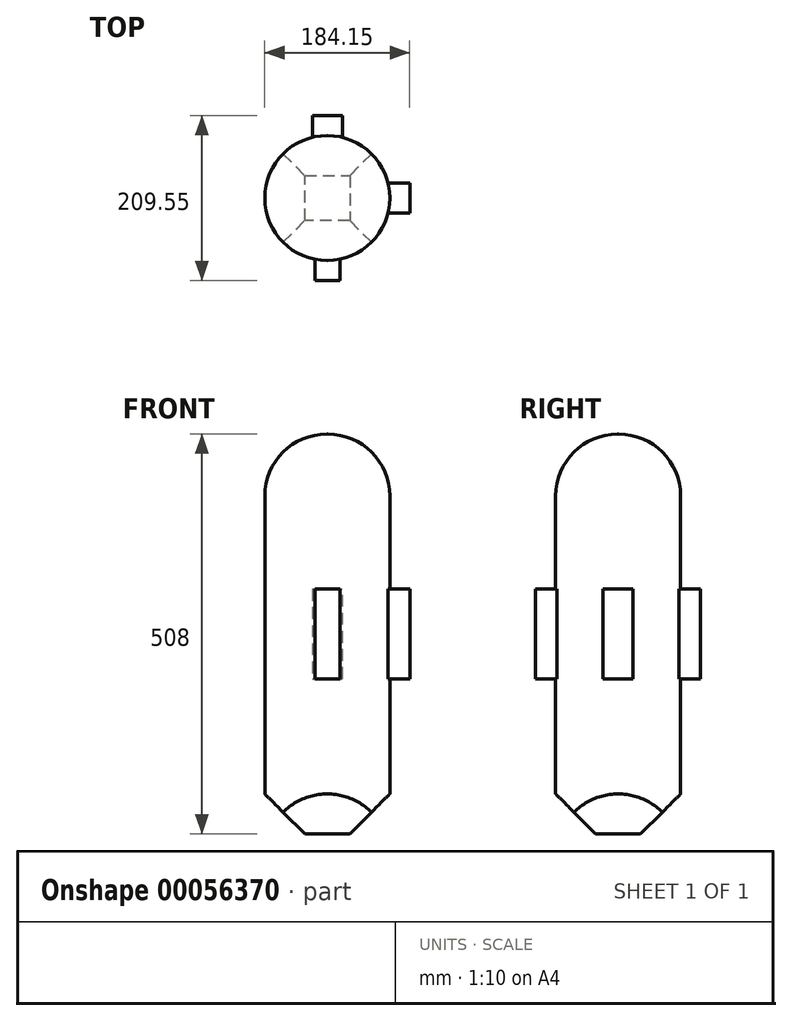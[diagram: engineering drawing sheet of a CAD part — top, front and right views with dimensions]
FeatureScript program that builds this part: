
annotation { "Feature Type Name" : "Feature", "Feature Type Description" : "" }
export const myFeature = defineFeature(function(context is Context, id is Id, definition is map)
    precondition{}
    {
        {
            var Q0;
            Q0=qCreatedBy(makeId("Front.planeOp"),FACE);
            var sketch = newSketch(context, id + "F0", { "sketchPlane" : qUnion([Q0])});
            skLineSegment(sketch, "E0.rect.bottom", {"start": v(79.37, -254) * mm, "end": v(-79.38, -254) * mm});
            skLineSegment(sketch, "E0.rect.top", {"start": v(79.37, 254) * mm, "end": v(-79.38, 254) * mm});
            skLineSegment(sketch, "E0.rect.left", {"start": v(79.37, -254) * mm, "end": v(79.37, 254) * mm});
            skLineSegment(sketch, "E0.rect.right", {"start": v(-79.38, -254) * mm, "end": v(-79.38, 254) * mm});
            skPoint(sketch, "E0.rect.middle", {"position": v(0, 0) * mm});
            skSolve(sketch);
        }
        {
            var Q0;
            Q0=makeQuery(id+"F0.imprint","IMPRINT",FACE,{"disambiguationData":[TD([[makeQuery(id+"F0.imprint","IMPRINT",EDGE,{"derivedFrom":sQuery(id+"F0.wireOp",EDGE,"E0.rect.bottom")}),-1.0]])]});
            extrude(context, id + "F1", {"entities" : qUnion([Q0]), "depth" : 158.75 * mm});
        }
        {
            var Q0;
            Q0=makeQuery(id+"F1.opExtrude","CAP_FACE",FACE,{"disambiguationData":[OSD([sQuery(id+"F0.wireOp",EDGE,"E0.rect.bottom"),sQuery(id+"F0.wireOp",EDGE,"E0.rect.top"),sQuery(id+"F0.wireOp",EDGE,"E0.rect.left"),sQuery(id+"F0.wireOp",EDGE,"E0.rect.right")])],"isStart":false});
            var sketch = newSketch(context, id + "F2", { "sketchPlane" : qUnion([Q0])});
            skLineSegment(sketch, "E1.rect.bottom", {"start": v(15.87, -57.15) * mm, "end": v(-15.88, -57.15) * mm});
            skLineSegment(sketch, "E1.rect.top", {"start": v(15.88, 57.15) * mm, "end": v(-15.87, 57.15) * mm});
            skLineSegment(sketch, "E1.rect.left", {"start": v(15.87, -57.15) * mm, "end": v(15.88, 57.15) * mm});
            skLineSegment(sketch, "E1.rect.right", {"start": v(-15.88, -57.15) * mm, "end": v(-15.87, 57.15) * mm});
            skPoint(sketch, "E1.rect.middle", {"position": v(0, 0) * mm});
            skSolve(sketch);
        }
        {
            var Q0;
            Q0=makeQuery(id+"F1.opExtrude","SWEPT_FACE",FACE,{"disambiguationData":[OSD([sQuery(id+"F0.wireOp",EDGE,"E0.rect.left")])]});
            var sketch = newSketch(context, id + "F3", { "sketchPlane" : qUnion([Q0])});
            skLineSegment(sketch, "E2.rect.bottom", {"start": v(-60.33, -57.15) * mm, "end": v(-98.43, -57.15) * mm});
            skLineSegment(sketch, "E2.rect.top", {"start": v(-60.33, 57.15) * mm, "end": v(-98.43, 57.15) * mm});
            skLineSegment(sketch, "E2.rect.left", {"start": v(-60.33, -57.15) * mm, "end": v(-60.33, 57.15) * mm});
            skLineSegment(sketch, "E2.rect.right", {"start": v(-98.43, -57.15) * mm, "end": v(-98.43, 57.15) * mm});
            skPoint(sketch, "E2.rect.middle", {"position": v(-79.38, 0) * mm});
            skPoint(sketch, "E2.rect.middle.positionSnap0", {"position": v(-79.38, 254) * mm});
            skPoint(sketch, "E2.rect.centerSnap0", {"position": v(-79.38, 254) * mm});
            skSolve(sketch);
        }
        {
            var Q0;
            Q0=makeQuery(id+"F3.imprint","IMPRINT",FACE,{"disambiguationData":[TD([[makeQuery(id+"F3.imprint","IMPRINT",EDGE,{"derivedFrom":sQuery(id+"F3.wireOp",EDGE,"E2.rect.bottom")}),-1.0]])]});
            extrude(context, id + "F4", {"entities" : qUnion([Q0]), "operationType" : NewBodyOperationType.ADD, "depth" : 25.4 * mm});
        }
        {
            var Q0;
            Q0=makeQuery(id+"F2.imprint","IMPRINT",FACE,{"disambiguationData":[TD([[makeQuery(id+"F2.imprint","IMPRINT",EDGE,{"derivedFrom":sQuery(id+"F2.wireOp",EDGE,"E1.rect.bottom")}),-1.0]])]});
            extrude(context, id + "F5", {"entities" : qUnion([Q0]), "operationType" : NewBodyOperationType.ADD, "depth" : 25.4 * mm});
        }
        {
            var Q0;
            Q0=makeQuery(id+"F1.opExtrude","SWEPT_FACE",FACE,{"disambiguationData":[OSD([sQuery(id+"F0.wireOp",EDGE,"E0.rect.top")])]});
            fillet(context, id + "F6", {"entities" : qUnion([Q0]), "radius" : 78.74 * mm, "tangentPropagation" : true, "allowEdgeOverflow" : false});
        }
        {
            var Q0;
            Q0=makeQuery(id+"F1.opExtrude","SWEPT_FACE",FACE,{"disambiguationData":[OSD([sQuery(id+"F0.wireOp",EDGE,"E0.rect.bottom")])]});
            chamfer(context, id + "F7", {"entities" : qUnion([Q0]), "width" : 50.8 * mm, "tangentPropagation" : true});
        }
        {
            var Q0;
            Q0=makeQuery(id+"F1.opExtrude","CAP_FACE",FACE,{"disambiguationData":[OSD([sQuery(id+"F0.wireOp",EDGE,"E0.rect.bottom"),sQuery(id+"F0.wireOp",EDGE,"E0.rect.top"),sQuery(id+"F0.wireOp",EDGE,"E0.rect.left"),sQuery(id+"F0.wireOp",EDGE,"E0.rect.right")])],"isStart":true});
            var sketch = newSketch(context, id + "F8", { "sketchPlane" : qUnion([Q0])});
            skLineSegment(sketch, "E3.rect.bottom", {"start": v(19.05, -57.15) * mm, "end": v(-19.05, -57.15) * mm});
            skLineSegment(sketch, "E3.rect.top", {"start": v(19.05, 57.15) * mm, "end": v(-19.05, 57.15) * mm});
            skLineSegment(sketch, "E3.rect.left", {"start": v(19.05, -57.15) * mm, "end": v(19.05, 57.15) * mm});
            skLineSegment(sketch, "E3.rect.right", {"start": v(-19.05, -57.15) * mm, "end": v(-19.05, 57.15) * mm});
            skPoint(sketch, "E3.rect.middle", {"position": v(0, 0) * mm});
            skSolve(sketch);
        }
        {
            var Q0;
            Q0=makeQuery(id+"F8.imprint","IMPRINT",FACE,{"disambiguationData":[TD([[makeQuery(id+"F8.imprint","IMPRINT",EDGE,{"derivedFrom":sQuery(id+"F8.wireOp",EDGE,"E3.rect.bottom")}),-1.0]])]});
            extrude(context, id + "F9", {"entities" : qUnion([Q0]), "operationType" : NewBodyOperationType.ADD, "depth" : 25.4 * mm});
        }
        {
            var Q0;
            Q0=makeQuery(id+"F1.opExtrude","CAP_EDGE",EDGE,{"disambiguationData":[OSD([sQuery(id+"F0.wireOp",EDGE,"E0.rect.left")])],"isStart":true});
            var Q1;
            Q1=makeQuery(id+"F1.opExtrude","CAP_EDGE",EDGE,{"disambiguationData":[OSD([sQuery(id+"F0.wireOp",EDGE,"E0.rect.right")])],"isStart":false});
            var Q2;
            Q2=makeQuery(id+"F1.opExtrude","CAP_EDGE",EDGE,{"disambiguationData":[OSD([sQuery(id+"F0.wireOp",EDGE,"E0.rect.right")])],"isStart":true});
            var Q3;
            Q3=makeQuery(id+"F1.opExtrude","CAP_EDGE",EDGE,{"disambiguationData":[OSD([sQuery(id+"F0.wireOp",EDGE,"E0.rect.left")])],"isStart":false});
            fillet(context, id + "F10", {"entities" : qUnion([Q0, Q1, Q2, Q3]), "radius" : 79.25 * mm, "tangentPropagation" : true, "allowEdgeOverflow" : false});
        }
    });
